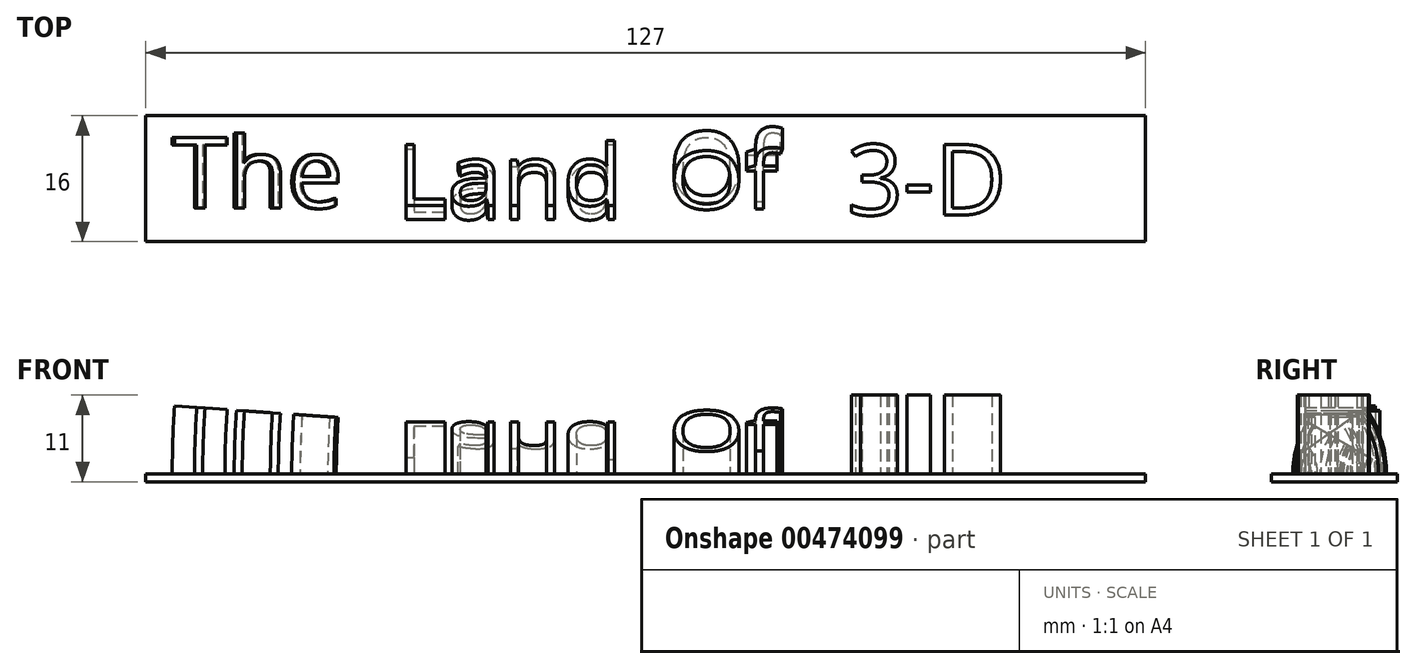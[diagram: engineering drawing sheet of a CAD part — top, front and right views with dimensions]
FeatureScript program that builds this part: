
annotation { "Feature Type Name" : "Feature", "Feature Type Description" : "" }
export const myFeature = defineFeature(function(context is Context, id is Id, definition is map)
    precondition{}
    {
        {
            var Q0;
            Q0=qCreatedBy(makeId("Top.planeOp"),FACE);
            var sketch = newSketch(context, id + "F0", { "sketchPlane" : qUnion([Q0])});
            skLineSegment(sketch, "E0.bottom", {"start": v(-63.5, 8) * mm, "end": v(63.5, 8) * mm});
            skLineSegment(sketch, "E0.top", {"start": v(-63.5, -8) * mm, "end": v(63.5, -8) * mm});
            skLineSegment(sketch, "E0.left", {"start": v(-63.5, 8) * mm, "end": v(-63.5, -8) * mm});
            skLineSegment(sketch, "E0.right", {"start": v(63.5, 8) * mm, "end": v(63.5, -8) * mm});
            skPoint(sketch, "E0.middle", {"position": v(0, 0) * mm});
            skSolve(sketch);
        }
        {
            var Q0;
            Q0=qSketchRegion(id+"F0",true);
            extrude(context, id + "F1", {"entities" : qUnion([Q0]), "depth" : 1 * mm});
        }
        {
            var Q0;
            Q0=makeQuery(id+"F1.opExtrude","CAP_FACE",FACE,{"disambiguationData":[OSD([sQuery(id+"F0.wireOp",EDGE,"E0.bottom"),sQuery(id+"F0.wireOp",EDGE,"E0.top"),sQuery(id+"F0.wireOp",EDGE,"E0.left"),sQuery(id+"F0.wireOp",EDGE,"E0.right")])],"isStart":false});
            var sketch = newSketch(context, id + "F2", { "sketchPlane" : qUnion([Q0])});
            skText(sketch, "E1", { "text": "The", "fontName": "OpenSans-Regular.ttf"});
            const initialGuessF2  = {"E1": [-0.06024, -0.00371, 1, 0, 0.009]};
            skSetInitialGuess(sketch, initialGuessF2);
            skSolve(sketch);
        }
        {
            var Q0;
            Q0=makeQuery(id+"F2.imprint","IMPRINT",FACE,{"disambiguationData":[TD([[makeQuery(id+"F2.imprint","IMPRINT",EDGE,{"derivedFrom":sQuery(id+"F2.wireOp",EDGE,"E1.sketch_text.stroke-0")}),1.0]])]});
            var sketch = newSketch(context, id + "F3", { "sketchPlane" : qUnion([Q0])});
            skText(sketch, "E2", { "text": "Land", "fontName": "OpenSans-Regular.ttf"});
            const initialGuessF3  = {"E2": [-0.03167, -0.00516, 1, 0, 0.009]};
            skSetInitialGuess(sketch, initialGuessF3);
            skSolve(sketch);
        }
        {
            var Q0;
            Q0=makeQuery(id+"F2.imprint","IMPRINT",FACE,{"disambiguationData":[TD([[makeQuery(id+"F2.imprint","IMPRINT",EDGE,{"derivedFrom":sQuery(id+"F2.wireOp",EDGE,"E1.sketch_text.stroke-0")}),1.0]])]});
            var sketch = newSketch(context, id + "F4", { "sketchPlane" : qUnion([Q0])});
            skText(sketch, "E3", { "text": "Of", "fontName": "OpenSans-Regular.ttf"});
            const initialGuessF4  = {"E3": [0.00287, -0.00294, 1, 0, 0.009]};
            skSetInitialGuess(sketch, initialGuessF4);
            skSolve(sketch);
        }
        {
            var Q0;
            Q0=makeQuery(id+"F2.imprint","IMPRINT",FACE,{"disambiguationData":[TD([[makeQuery(id+"F2.imprint","IMPRINT",EDGE,{"derivedFrom":sQuery(id+"F2.wireOp",EDGE,"E1.sketch_text.stroke-0")}),1.0]])]});
            var sketch = newSketch(context, id + "F5", { "sketchPlane" : qUnion([Q0])});
            skText(sketch, "E4", { "text": "3-D", "fontName": "OpenSans-Regular.ttf"});
            const initialGuessF5  = {"E4": [0.02555, -0.0046, 1, 0, 0.009]};
            skSetInitialGuess(sketch, initialGuessF5);
            skSolve(sketch);
        }
        {
            var Q0;
            Q0=qSketchRegion(id+"F5",true);
            extrude(context, id + "F6", {"entities" : qUnion([Q0]), "operationType" : NewBodyOperationType.ADD, "depth" : 10 * mm});
        }
        {
            var Q0;
            Q0=qSketchRegion(id+"F4",true);
            var Q1;
            Q1=makeQuery(id+"F1.opExtrude","CAP_EDGE",EDGE,{"disambiguationData":[OSD([sQuery(id+"F0.wireOp",EDGE,"E0.top")])],"isStart":false});
            revolve(context, id + "F7", {"operationType" : NewBodyOperationType.ADD, "entities" : qUnion([Q0]), "axis" : qUnion([Q1]), "revolveType" : RevolveType.ONE_DIRECTION, "angle" : 35 * degree});
        }
        {
            var Q0;
            Q0=qSketchRegion(id+"F2",true);
            var Q1;
            Q1=makeQuery(id+"F1.opExtrude","CAP_EDGE",EDGE,{"disambiguationData":[OSD([sQuery(id+"F0.wireOp",EDGE,"E0.right")])],"isStart":false});
            revolve(context, id + "F8", {"operationType" : NewBodyOperationType.ADD, "entities" : qUnion([Q0]), "axis" : qUnion([Q1]), "revolveType" : RevolveType.ONE_DIRECTION, "oppositeDirection" : true, "angle" : 4 * degree});
        }
        {
            var Q0;
            Q0=qSketchRegion(id+"F3",true);
            var Q1;
            Q1=makeQuery(id+"F1.opExtrude","CAP_EDGE",EDGE,{"disambiguationData":[OSD([sQuery(id+"F0.wireOp",EDGE,"E0.bottom")])],"isStart":false});
            revolve(context, id + "F9", {"operationType" : NewBodyOperationType.ADD, "entities" : qUnion([Q0]), "axis" : qUnion([Q1]), "revolveType" : RevolveType.ONE_DIRECTION, "oppositeDirection" : true, "angle" : 30 * degree});
        }
    });
